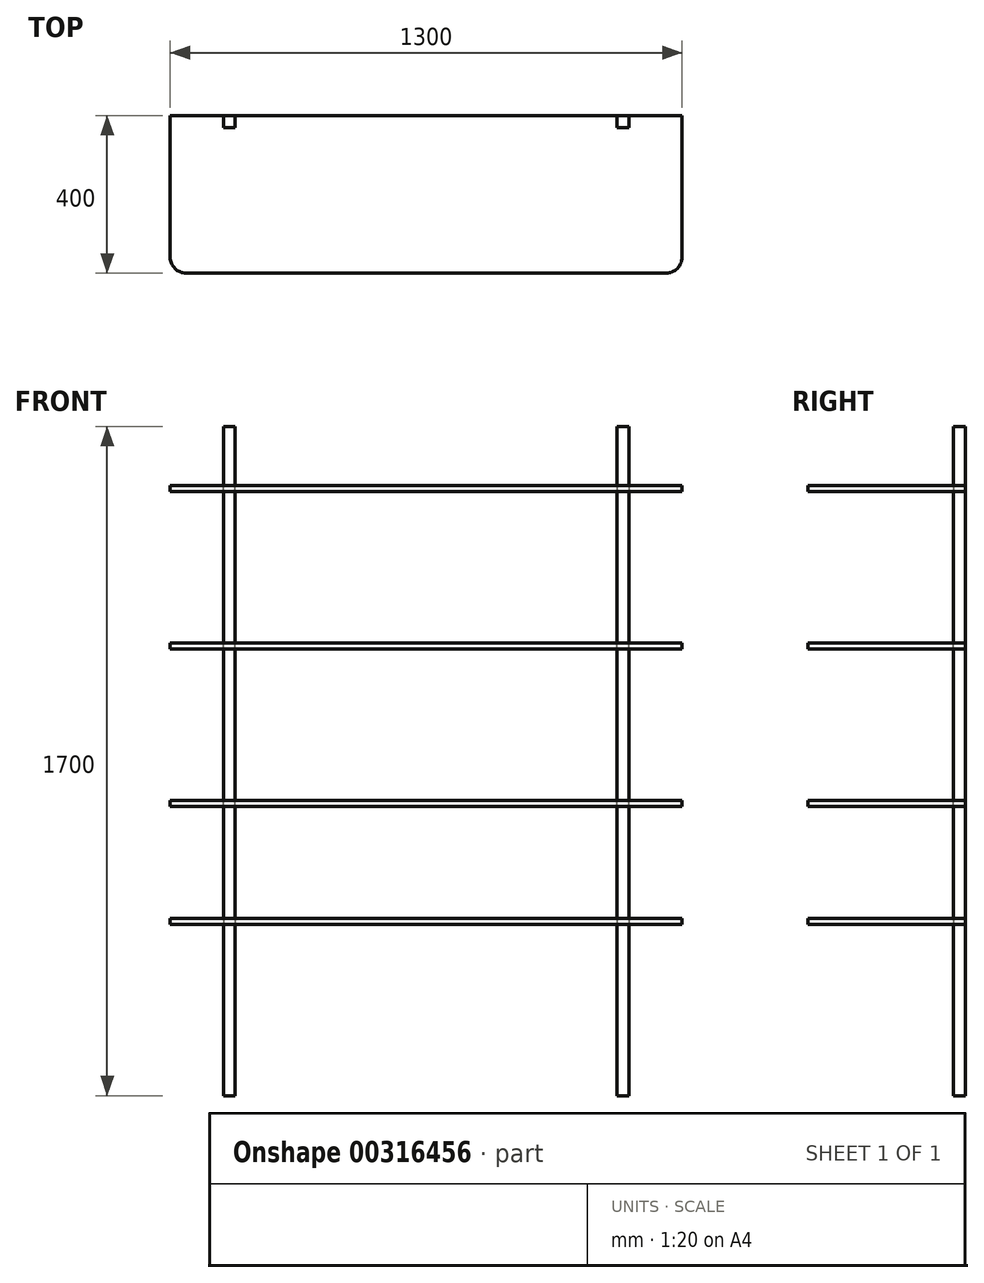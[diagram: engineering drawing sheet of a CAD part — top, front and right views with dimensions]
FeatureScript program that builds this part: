
annotation { "Feature Type Name" : "Feature", "Feature Type Description" : "" }
export const myFeature = defineFeature(function(context is Context, id is Id, definition is map)
    precondition{}
    {
        {
            assignVariable(context, id + "F0", {"name" : "Hauteur", "anyValue" : 1700});
        }
        {
            assignVariable(context, id + "F1", {"name" : "Ep", "anyValue" : 15});
        }
        {
            assignVariable(context, id + "F2", {"name" : "Niveau1", "anyValue" : 450});
        }
        {
            assignVariable(context, id + "F3", {"name" : "Niveau2", "anyValue" : 750});
        }
        {
            assignVariable(context, id + "F4", {"name" : "Niveau3", "anyValue" : 1150});
        }
        {
            assignVariable(context, id + "F5", {"name" : "Niveau4", "anyValue" : 1550});
        }
        {
            assignVariable(context, id + "F6", {"name" : "Niveau5", "anyValue" : 2000});
        }
        {
            var Q0;
            Q0=qCreatedBy(makeId("Top.planeOp"),FACE);
            var sketch = newSketch(context, id + "F7", { "sketchPlane" : qUnion([Q0])});
            skLineSegment(sketch, "E0.bottom", {"start": v(-515, 0) * mm, "end": v(-485, 0) * mm});
            skLineSegment(sketch, "E0.top", {"start": v(-515, -30) * mm, "end": v(-485, -30) * mm});
            skLineSegment(sketch, "E0.left", {"start": v(-515, 0) * mm, "end": v(-515, -30) * mm});
            skLineSegment(sketch, "E0.right", {"start": v(-485, 0) * mm, "end": v(-485, -30) * mm});
            skLineSegment(sketch, "E1", {"start": v(0, 0) * mm, "end": v(0, -268.34) * mm, "construction": true});
            skLineSegment(sketch, "E2.MirrorCS", {"start": v(515, 0) * mm, "end": v(485, 0) * mm});
            skLineSegment(sketch, "E3.MirrorCS", {"start": v(515, -30) * mm, "end": v(485, -30) * mm});
            skLineSegment(sketch, "E4.MirrorCS", {"start": v(515, 0) * mm, "end": v(515, -30) * mm});
            skLineSegment(sketch, "E5.MirrorCS", {"start": v(485, 0) * mm, "end": v(485, -30) * mm});
            skSolve(sketch);
        }
        {
            var Q0;
            Q0=makeQuery(id+"F7.imprint","IMPRINT",FACE,{"disambiguationData":[TD([[makeQuery(id+"F7.imprint","IMPRINT",EDGE,{"derivedFrom":sQuery(id+"F7.wireOp",EDGE,"E0.bottom")}),-1.0]])]});
            var Q1;
            Q1=makeQuery(id+"F7.imprint","IMPRINT",FACE,{"disambiguationData":[TD([[makeQuery(id+"F7.imprint","IMPRINT",EDGE,{"derivedFrom":sQuery(id+"F7.wireOp",EDGE,"E2.MirrorCS")}),1.0]])]});
            extrude(context, id + "F8", {"entities" : qUnion([Q0, Q1]), "depth" : (getVariable(context, 'Hauteur')) * mm});
        }
        {
            var Q0;
            Q0=qCreatedBy(makeId("Top.planeOp"),FACE);
            cPlane(context, id + "F9", {"entities" : qUnion([Q0]), "cplaneType" : CPlaneType.OFFSET, "offset" : (getVariable(context, 'Niveau1')) * mm, "width" : 150 * mm, "height" : 150 * mm});
        }
        {
            var Q0;
            Q0=qCreatedBy(makeId("Top.planeOp"),FACE);
            cPlane(context, id + "F10", {"entities" : qUnion([Q0]), "cplaneType" : CPlaneType.OFFSET, "offset" : (getVariable(context, 'Niveau2')) * mm, "width" : 150 * mm, "height" : 150 * mm});
        }
        {
            var Q0;
            Q0=qCreatedBy(makeId("Top.planeOp"),FACE);
            cPlane(context, id + "F11", {"entities" : qUnion([Q0]), "cplaneType" : CPlaneType.OFFSET, "offset" : (getVariable(context, 'Niveau3')) * mm, "width" : 150 * mm, "height" : 150 * mm});
        }
        {
            var Q0;
            Q0=qCreatedBy(makeId("Top.planeOp"),FACE);
            cPlane(context, id + "F12", {"entities" : qUnion([Q0]), "cplaneType" : CPlaneType.OFFSET, "offset" : (getVariable(context, 'Niveau4')) * mm, "width" : 150 * mm, "height" : 150 * mm});
        }
        {
            var Q0;
            Q0=qCreatedBy(makeId("Top.planeOp"),FACE);
            cPlane(context, id + "F13", {"entities" : qUnion([Q0]), "cplaneType" : CPlaneType.OFFSET, "offset" : (getVariable(context, 'Niveau5')) * mm, "width" : 150 * mm, "height" : 150 * mm});
        }
        {
            var Q0;
            Q0=qCreatedBy(id+"F9.planeOp",FACE);
            var sketch = newSketch(context, id + "F14", { "sketchPlane" : qUnion([Q0])});
            skLineSegment(sketch, "E6", {"start": v(0, 0) * mm, "end": v(0, -284.12) * mm, "construction": true});
            skLineSegment(sketch, "E7", {"start": v(0, 0) * mm, "end": v(-485, 0) * mm});
            skLineSegment(sketch, "E8", {"start": v(-650, 0) * mm, "end": v(-650, -360) * mm});
            skLineSegment(sketch, "E9", {"start": v(-610, -400) * mm, "end": v(0, -400) * mm});
            skPoint(sketch, "E10.visualSharp", {"position": v(-650, -400) * mm});
            skArc(sketch, "E10.filletArc", {"start": v(-650, -360) * mm, "mid": v(-638.28, -388.28) * mm, "end": v(-610, -400) * mm});
            skLineSegment(sketch, "E11.0", {"start": v(-515, 0) * mm, "end": v(-515, -30) * mm});
            skLineSegment(sketch, "E12.0", {"start": v(-515, -30) * mm, "end": v(-485, -30) * mm});
            skLineSegment(sketch, "E13.0", {"start": v(-485, 0) * mm, "end": v(-485, -30) * mm});
            skLineSegment(sketch, "E14.trimOffspring", {"start": v(-515, 0) * mm, "end": v(-650, 0) * mm});
            skLineSegment(sketch, "E15.MirrorCS", {"start": v(0, 0) * mm, "end": v(485, 0) * mm});
            skLineSegment(sketch, "E16.MirrorCS", {"start": v(485, 0) * mm, "end": v(485, -30) * mm});
            skLineSegment(sketch, "E17.MirrorCS", {"start": v(515, -30) * mm, "end": v(485, -30) * mm});
            skLineSegment(sketch, "E18.MirrorCS", {"start": v(515, 0) * mm, "end": v(515, -30) * mm});
            skLineSegment(sketch, "E19.MirrorCS", {"start": v(515, 0) * mm, "end": v(650, 0) * mm});
            skLineSegment(sketch, "E20.MirrorCS", {"start": v(650, 0) * mm, "end": v(650, -360) * mm});
            skArc(sketch, "E21.MirrorCS", {"start": v(650, -360) * mm, "mid": v(638.28, -388.28) * mm, "end": v(610, -400) * mm});
            skLineSegment(sketch, "E22.MirrorCS", {"start": v(610, -400) * mm, "end": v(0, -400) * mm});
            skSolve(sketch);
        }
        {
            var Q0;
            Q0=makeQuery(id+"F14.imprint","IMPRINT",FACE,{"disambiguationData":[TD([[makeQuery(id+"F14.imprint","IMPRINT",EDGE,{"derivedFrom":sQuery(id+"F14.wireOp",EDGE,"E7")}),1.0]])]});
            extrude(context, id + "F15", {"entities" : qUnion([Q0]), "oppositeDirection" : true, "depth" : (getVariable(context, 'Ep')) * mm});
        }
        {
            var Q0;
            Q0=qCreatedBy(id+"F10.planeOp",FACE);
            var sketch = newSketch(context, id + "F16", { "sketchPlane" : qUnion([Q0])});
            skLineSegment(sketch, "E23.0", {"start": v(610, -400) * mm, "end": v(0, -400) * mm});
            skLineSegment(sketch, "E23.1", {"start": v(515, 0) * mm, "end": v(650, 0) * mm});
            skLineSegment(sketch, "E23.2", {"start": v(650, 0) * mm, "end": v(650, -360) * mm});
            skLineSegment(sketch, "E23.4", {"start": v(0, 0) * mm, "end": v(-485, 0) * mm});
            skLineSegment(sketch, "E23.5", {"start": v(-650, 0) * mm, "end": v(-650, -360) * mm});
            skLineSegment(sketch, "E23.6", {"start": v(-610, -400) * mm, "end": v(0, -400) * mm});
            skLineSegment(sketch, "E23.7", {"start": v(-515, 0) * mm, "end": v(-650, 0) * mm});
            skLineSegment(sketch, "E23.8", {"start": v(0, 0) * mm, "end": v(485, 0) * mm});
            skLineSegment(sketch, "E23.9", {"start": v(650, 0) * mm, "end": v(650, -360) * mm});
            skArc(sketch, "E24.0", {"start": v(-650, -360) * mm, "mid": v(-638.28, -388.28) * mm, "end": v(-610, -400) * mm});
            skArc(sketch, "E25.0", {"start": v(650, -360) * mm, "mid": v(638.28, -388.28) * mm, "end": v(610, -400) * mm});
            skLineSegment(sketch, "E26.0", {"start": v(-515, -30) * mm, "end": v(-485, -30) * mm});
            skLineSegment(sketch, "E27.0", {"start": v(-515, 0) * mm, "end": v(-515, -30) * mm});
            skLineSegment(sketch, "E28.0", {"start": v(-485, 0) * mm, "end": v(-485, -30) * mm});
            skLineSegment(sketch, "E29.0", {"start": v(485, 0) * mm, "end": v(485, -30) * mm});
            skLineSegment(sketch, "E30.0", {"start": v(515, -30) * mm, "end": v(485, -30) * mm});
            skPoint(sketch, "E31.0", {"position": v(515, -15) * mm});
            skLineSegment(sketch, "E32.0", {"start": v(515, 0) * mm, "end": v(515, -30) * mm});
            skSolve(sketch);
        }
        {
            var Q0;
            Q0=makeQuery(id+"F16.imprint","IMPRINT",FACE,{"disambiguationData":[TD([[makeQuery(id+"F16.imprint","IMPRINT",EDGE,{"derivedFrom":sQuery(id+"F16.wireOp",EDGE,"E23.0")}),-1.0]])]});
            extrude(context, id + "F17", {"entities" : qUnion([Q0]), "oppositeDirection" : true, "depth" : (getVariable(context, 'Ep')) * mm});
        }
        {
            var Q0;
            Q0=qCreatedBy(id+"F11.planeOp",FACE);
            var sketch = newSketch(context, id + "F18", { "sketchPlane" : qUnion([Q0])});
            skLineSegment(sketch, "E33.0", {"start": v(610, -400) * mm, "end": v(0, -400) * mm});
            skLineSegment(sketch, "E33.1", {"start": v(515, 0) * mm, "end": v(650, 0) * mm});
            skLineSegment(sketch, "E33.2", {"start": v(650, 0) * mm, "end": v(650, -360) * mm});
            skLineSegment(sketch, "E33.4", {"start": v(0, 0) * mm, "end": v(-485, 0) * mm});
            skLineSegment(sketch, "E33.5", {"start": v(-650, 0) * mm, "end": v(-650, -360) * mm});
            skLineSegment(sketch, "E33.6", {"start": v(-610, -400) * mm, "end": v(0, -400) * mm});
            skLineSegment(sketch, "E33.7", {"start": v(-515, 0) * mm, "end": v(-650, 0) * mm});
            skLineSegment(sketch, "E33.8", {"start": v(0, 0) * mm, "end": v(485, 0) * mm});
            skLineSegment(sketch, "E33.9", {"start": v(650, 0) * mm, "end": v(650, -360) * mm});
            skLineSegment(sketch, "E33.10", {"start": v(-610, -400) * mm, "end": v(610, -400) * mm});
            skArc(sketch, "E34.0", {"start": v(-650, -360) * mm, "mid": v(-638.28, -388.28) * mm, "end": v(-610, -400) * mm});
            skLineSegment(sketch, "E35.0", {"start": v(-515, 0) * mm, "end": v(-515, -30) * mm});
            skLineSegment(sketch, "E36.0", {"start": v(-515, -30) * mm, "end": v(-485, -30) * mm});
            skLineSegment(sketch, "E37.0", {"start": v(-485, 0) * mm, "end": v(-485, -30) * mm});
            skLineSegment(sketch, "E38.0", {"start": v(485, 0) * mm, "end": v(485, -30) * mm});
            skLineSegment(sketch, "E39.0", {"start": v(515, -30) * mm, "end": v(485, -30) * mm});
            skLineSegment(sketch, "E40.0", {"start": v(515, 0) * mm, "end": v(515, -30) * mm});
            skArc(sketch, "E41.0", {"start": v(650, -360) * mm, "mid": v(638.28, -388.28) * mm, "end": v(610, -400) * mm});
            skSolve(sketch);
        }
        {
            var Q0;
            Q0=makeQuery(id+"F18.imprint","IMPRINT",FACE,{"disambiguationData":[TD([[makeQuery(id+"F18.imprint","IMPRINT",EDGE,{"derivedFrom":sQuery(id+"F18.wireOp",EDGE,"E33.1")}),-1.0]])]});
            extrude(context, id + "F19", {"entities" : qUnion([Q0]), "oppositeDirection" : true, "depth" : (getVariable(context, 'Ep')) * mm});
        }
        {
            var Q0;
            Q0=qCreatedBy(id+"F12.planeOp",FACE);
            var sketch = newSketch(context, id + "F20", { "sketchPlane" : qUnion([Q0])});
            skPoint(sketch, "E42.0", {"position": v(610, -400) * mm});
            skLineSegment(sketch, "E43.0", {"start": v(610, -400) * mm, "end": v(0, -400) * mm});
            skLineSegment(sketch, "E43.1", {"start": v(515, 0) * mm, "end": v(650, 0) * mm});
            skLineSegment(sketch, "E43.2", {"start": v(650, 0) * mm, "end": v(650, -360) * mm});
            skArc(sketch, "E43.3", {"start": v(650, -360) * mm, "mid": v(638.28, -388.28) * mm, "end": v(610, -400) * mm});
            skLineSegment(sketch, "E43.5", {"start": v(0, 0) * mm, "end": v(-485, 0) * mm});
            skLineSegment(sketch, "E43.6", {"start": v(-650, 0) * mm, "end": v(-650, -360) * mm});
            skLineSegment(sketch, "E43.7", {"start": v(-610, -400) * mm, "end": v(0, -400) * mm});
            skLineSegment(sketch, "E43.8", {"start": v(-515, 0) * mm, "end": v(-650, 0) * mm});
            skLineSegment(sketch, "E43.9", {"start": v(0, 0) * mm, "end": v(485, 0) * mm});
            skLineSegment(sketch, "E43.10", {"start": v(650, 0) * mm, "end": v(650, -360) * mm});
            skLineSegment(sketch, "E43.11", {"start": v(-610, -400) * mm, "end": v(610, -400) * mm});
            skArc(sketch, "E43.12", {"start": v(650, -360) * mm, "mid": v(638.28, -388.28) * mm, "end": v(610, -400) * mm});
            skLineSegment(sketch, "E44.0", {"start": v(515, 0) * mm, "end": v(515, -30) * mm});
            skLineSegment(sketch, "E45.0", {"start": v(515, -30) * mm, "end": v(485, -30) * mm});
            skLineSegment(sketch, "E46.0", {"start": v(485, 0) * mm, "end": v(485, -30) * mm});
            skLineSegment(sketch, "E47.0", {"start": v(-515, 0) * mm, "end": v(-515, -30) * mm});
            skLineSegment(sketch, "E48.0", {"start": v(-515, -30) * mm, "end": v(-485, -30) * mm});
            skLineSegment(sketch, "E49.0", {"start": v(-485, 0) * mm, "end": v(-485, -30) * mm});
            skPoint(sketch, "E50.0", {"position": v(-638.28, -388.28) * mm});
            skArc(sketch, "E51.0", {"start": v(-650, -360) * mm, "mid": v(-638.28, -388.28) * mm, "end": v(-610, -400) * mm});
            skSolve(sketch);
        }
        {
            var Q0;
            Q0=makeQuery(id+"F20.imprint","IMPRINT",FACE,{"disambiguationData":[TD([[makeQuery(id+"F20.imprint","IMPRINT",EDGE,{"derivedFrom":sQuery(id+"F20.wireOp",EDGE,"E43.1")}),-1.0]])]});
            extrude(context, id + "F21", {"entities" : qUnion([Q0]), "oppositeDirection" : true, "depth" : (getVariable(context, 'Ep')) * mm});
        }
    });
